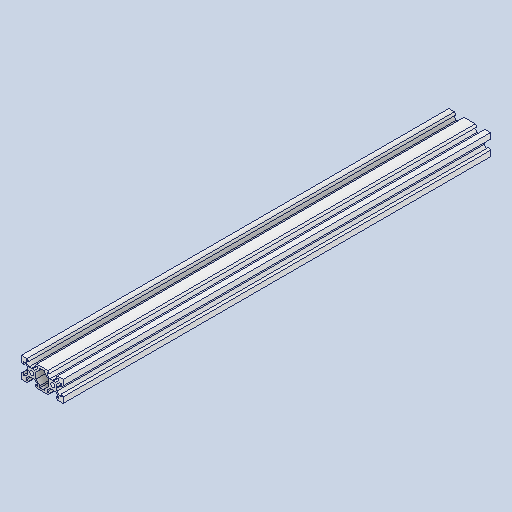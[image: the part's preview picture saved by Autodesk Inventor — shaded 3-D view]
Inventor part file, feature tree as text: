
AUTODESK INVENTOR PART (.ipt)
format: ipt  version: 2025.2 (Build 292293000, 293)  size: 387,584 bytes
history: native  units: in
note: dims shown in document units (in); Inventor stores cm internally (conversion verified against a paired STEP export)
features: plane x2, extrude x1, sketch x1, other x1
ambient origin geometry x8: Origin, YZ Plane, XZ Plane, XY Plane, X Axis, Y Axis, Z Axis, Center Point
bodies: Solid1 (feature_tree)
feature tree (5):
  extrude  "Extrusion1"  [1 undecoded]
  plane  "Work Plane1"
  plane  "Work Plane2"
  sketch  "Sketch1"  dims[d0=3.5433in d1=0.0in d2=-8.0709in]
  other  "Boss-Extrude1"
note: 1 required parameter value undecoded (feature->parameter linkage not recoverable at this tier; creation-order binding heuristic only, values carry confidence <= 0.55)
